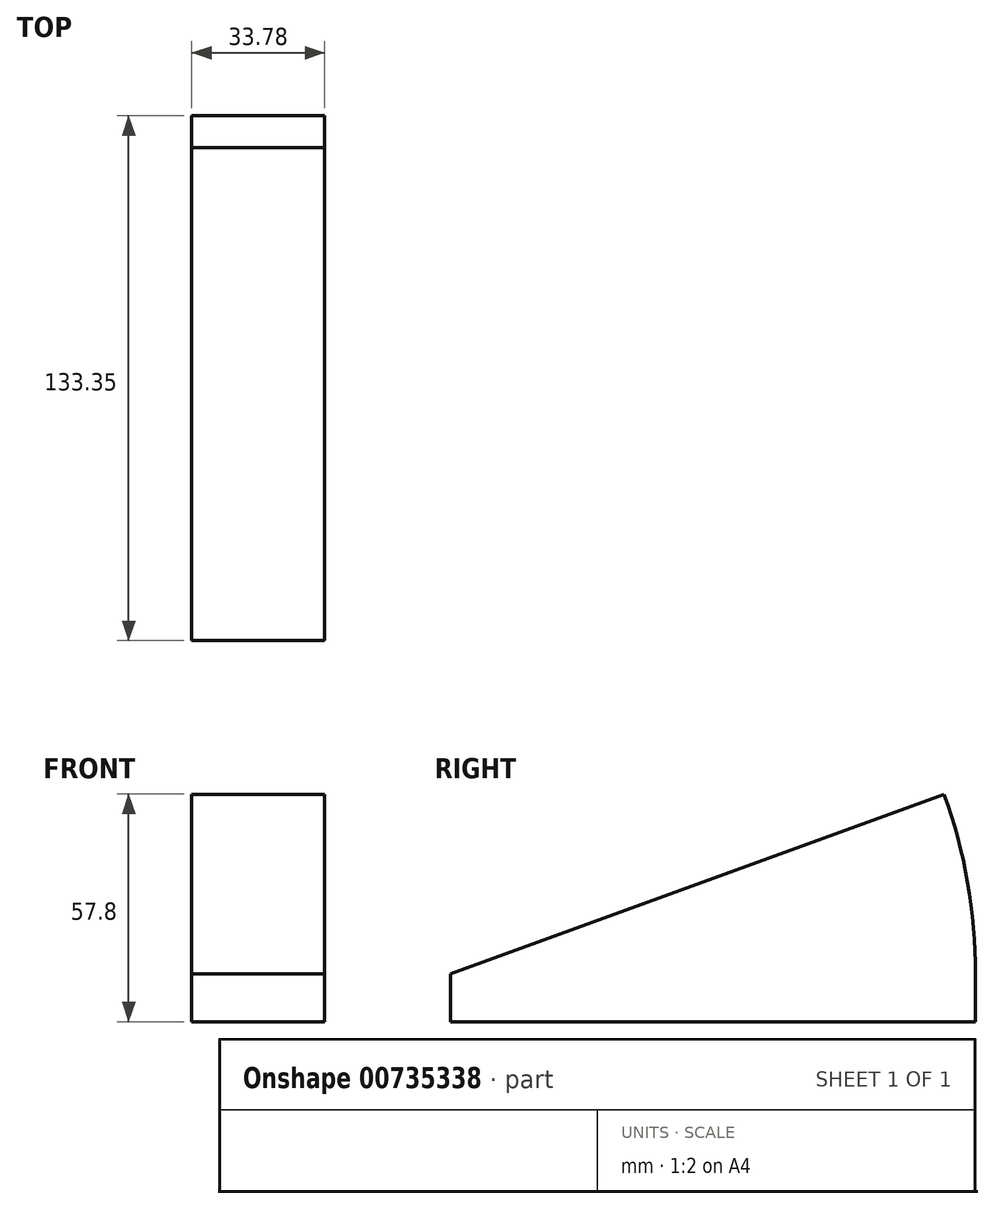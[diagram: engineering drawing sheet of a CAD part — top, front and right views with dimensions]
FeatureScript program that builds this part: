
annotation { "Feature Type Name" : "Feature", "Feature Type Description" : "" }
export const myFeature = defineFeature(function(context is Context, id is Id, definition is map)
    precondition{}
    {
        {
            var Q0;
            Q0=qCreatedBy(makeId("Top.planeOp"),FACE);
            var sketch = newSketch(context, id + "F0", { "sketchPlane" : qUnion([Q0])});
            skLineSegment(sketch, "E0.bottom", {"start": v(-42.36, 103.78) * mm, "end": v(-8.58, 103.78) * mm});
            skLineSegment(sketch, "E0.top", {"start": v(-42.36, -29.57) * mm, "end": v(-8.58, -29.57) * mm});
            skLineSegment(sketch, "E0.left", {"start": v(-42.36, 103.78) * mm, "end": v(-42.36, -29.57) * mm});
            skLineSegment(sketch, "E0.right", {"start": v(-8.58, 103.78) * mm, "end": v(-8.58, -29.57) * mm});
            skSolve(sketch);
        }
        {
            var Q0;
            Q0=makeQuery(id+"F0.imprint","IMPRINT",FACE,{"disambiguationData":[TD([[makeQuery(id+"F0.imprint","IMPRINT",EDGE,{"derivedFrom":sQuery(id+"F0.wireOp",EDGE,"E0.bottom")}),-1.0]])]});
            var Q1;
            Q1=sQuery(id+"F0.wireOp",EDGE,"E0.top");
            revolve(context, id + "F1", {"surfaceOperationType" : NewSurfaceOperationType.NEW, "entities" : qUnion([Q0]), "axis" : qUnion([Q1]), "revolveType" : RevolveType.ONE_DIRECTION, "angle" : 20 * degree});
        }
        {
            var Q0;
            Q0 = qSketchRegion(id + "F0", true);
            extrude(context, id + "F2", {"entities" : qUnion([Q0]), "operationType" : NewBodyOperationType.ADD, "oppositeDirection" : true, "depth" : 12.2 * mm, "offsetDistance" : 25.4 * mm});
        }
    });
